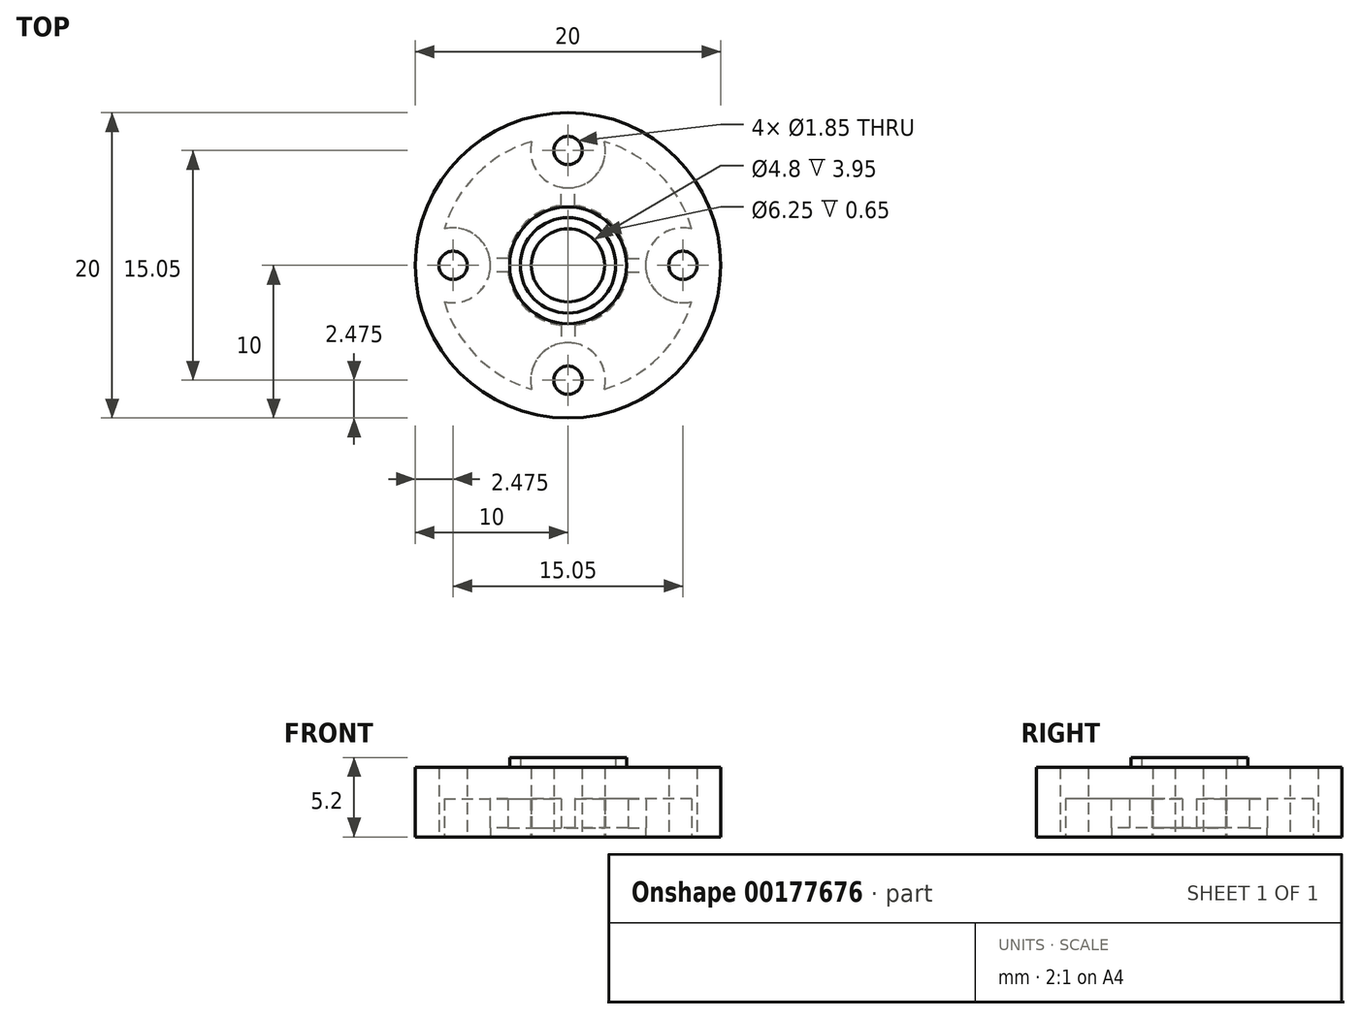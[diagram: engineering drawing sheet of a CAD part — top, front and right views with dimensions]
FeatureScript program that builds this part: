
annotation { "Feature Type Name" : "Feature", "Feature Type Description" : "" }
export const myFeature = defineFeature(function(context is Context, id is Id, definition is map)
    precondition{}
    {
        {
            var Q0;
            Q0=qCreatedBy(makeId("Top.planeOp"),FACE);
            var sketch = newSketch(context, id + "F0", { "sketchPlane" : qUnion([Q0])});
            skCircle(sketch, "E0", {"center": v(0, 0) * mm, "radius": 10 * mm});
            skSolve(sketch);
        }
        {
            var Q0;
            Q0=qSketchRegion(id+"F0",true);
            extrude(context, id + "F1", {"entities" : qUnion([Q0]), "depth" : 4.55 * mm});
        }
        {
            var Q0;
            Q0=makeQuery(id+"F1.opExtrude","CAP_FACE",FACE,{"disambiguationData":[OSD([sQuery(id+"F0.wireOp",EDGE,"E0")])],"isStart":true});
            var sketch = newSketch(context, id + "F2", { "sketchPlane" : qUnion([Q0])});
            skCircle(sketch, "E1", {"center": v(0, 0) * mm, "radius": 8.45 * mm});
            skCircle(sketch, "E2", {"center": v(0, 0) * mm, "radius": 3.95 * mm});
            skCircle(sketch, "E3", {"center": v(0, 0) * mm, "radius": 2.4 * mm});
            skLineSegment(sketch, "E4", {"start": v(0, 8.45) * mm, "end": v(0, -8.45) * mm, "construction": true});
            skLineSegment(sketch, "E5", {"start": v(8.45, 0) * mm, "end": v(-8.45, 0) * mm, "construction": true});
            skLineSegment(sketch, "E6", {"start": v(0.45, 3.92) * mm, "end": v(0.45, 5.12) * mm});
            skLineSegment(sketch, "E7", {"start": v(-0.45, 3.92) * mm, "end": v(-0.45, 5.12) * mm});
            skLineSegment(sketch, "E8", {"start": v(3.92, 0.45) * mm, "end": v(5.12, 0.45) * mm});
            skLineSegment(sketch, "E9", {"start": v(3.92, -0.45) * mm, "end": v(5.12, -0.45) * mm});
            skLineSegment(sketch, "E10", {"start": v(0.45, -3.92) * mm, "end": v(0.45, -5.12) * mm});
            skLineSegment(sketch, "E11", {"start": v(-0.45, -3.92) * mm, "end": v(-0.45, -5.12) * mm});
            skLineSegment(sketch, "E12", {"start": v(-3.92, -0.45) * mm, "end": v(-5.12, -0.45) * mm});
            skLineSegment(sketch, "E13", {"start": v(-3.92, 0.45) * mm, "end": v(-5.12, 0.45) * mm});
            skCircle(sketch, "E14", {"center": v(7.52, 0) * mm, "radius": 0.93 * mm});
            skCircle(sketch, "E15", {"center": v(7.52, 0) * mm, "radius": 2.45 * mm});
            skCircle(sketch, "E16.1.0", {"center": v(0, 7.52) * mm, "radius": 0.93 * mm});
            skCircle(sketch, "E16.1.1", {"center": v(0, 7.52) * mm, "radius": 2.45 * mm});
            skCircle(sketch, "E16.2.0", {"center": v(-7.52, 0) * mm, "radius": 0.93 * mm});
            skCircle(sketch, "E16.2.1", {"center": v(-7.52, 0) * mm, "radius": 2.45 * mm});
            skCircle(sketch, "E16.3.0", {"center": v(0, -7.52) * mm, "radius": 0.93 * mm});
            skCircle(sketch, "E16.3.1", {"center": v(0, -7.52) * mm, "radius": 2.45 * mm});
            skLineSegment(sketch, "E17.trimOffspring", {"start": v(8.33, -0.45) * mm, "end": v(8.44, -0.45) * mm});
            skLineSegment(sketch, "E18.trimOffspring", {"start": v(8.33, 0.45) * mm, "end": v(8.44, 0.45) * mm});
            skLineSegment(sketch, "E19.trimOffspring", {"start": v(-0.45, -8.33) * mm, "end": v(-0.45, -8.44) * mm});
            skLineSegment(sketch, "E20.trimOffspring", {"start": v(0.45, -8.33) * mm, "end": v(0.45, -8.44) * mm});
            skLineSegment(sketch, "E21.trimOffspring", {"start": v(-8.33, -0.45) * mm, "end": v(-8.44, -0.45) * mm});
            skLineSegment(sketch, "E22.trimOffspring", {"start": v(-8.33, 0.45) * mm, "end": v(-8.44, 0.45) * mm});
            skLineSegment(sketch, "E23.trimOffspring", {"start": v(-0.45, 8.33) * mm, "end": v(-0.45, 8.44) * mm});
            skLineSegment(sketch, "E24.trimOffspring", {"start": v(0.45, 8.33) * mm, "end": v(0.45, 8.44) * mm});
            skSolve(sketch);
        }
        {
            var Q0;
            {var subQ6=sQuery(id+"F2.wireOp",EDGE,"E6");Q0=makeQuery(id+"F2.imprint","IMPRINT",FACE,{"disambiguationData":[TD([[makeQuery(id+"F2.imprint","IMPRINT",EDGE,{"derivedFrom":subQ6}),-1.0]])]});}
            var Q1;
            {var subQ6=sQuery(id+"F2.wireOp",EDGE,"E7");Q1=makeQuery(id+"F2.imprint","IMPRINT",FACE,{"disambiguationData":[TD([[makeQuery(id+"F2.imprint","IMPRINT",EDGE,{"derivedFrom":subQ6}),1.0]])]});}
            var Q2;
            {var subQ0=sQuery(id+"F2.wireOp",EDGE,"E11");Q2=makeQuery(id+"F2.imprint","IMPRINT",FACE,{"disambiguationData":[TD([[makeQuery(id+"F2.imprint","IMPRINT",EDGE,{"derivedFrom":subQ0}),-1.0]])]});}
            var Q3;
            {var subQ1=sQuery(id+"F2.wireOp",EDGE,"E9");Q3=makeQuery(id+"F2.imprint","IMPRINT",FACE,{"disambiguationData":[TD([[makeQuery(id+"F2.imprint","IMPRINT",EDGE,{"derivedFrom":subQ1}),-1.0]])]});}
            var Q4;
            {var subQ0=sQuery(id+"F2.wireOp",EDGE,"E14");var subQ1=makeQuery(id+"F2.imprint","INTERSECT",VERTEX,{"derivedFrom":[subQ0,sQuery(id+"F2.wireOp",EDGE,"E18.trimOffspring")]});Q4=makeQuery(id+"F2.imprint","IMPRINT",FACE,{"disambiguationData":[TD([[makeQuery(id+"F2.imprint","IMPRINT",EDGE,{"disambiguationData":[TD([[subQ1,1.0]])],"derivedFrom":subQ0}),1.0]])]});}
            var Q5;
            {var subQ0=sQuery(id+"F2.wireOp",EDGE,"E16.2.0");var subQ1=makeQuery(id+"F2.imprint","INTERSECT",VERTEX,{"derivedFrom":[subQ0,sQuery(id+"F2.wireOp",EDGE,"E21.trimOffspring")]});Q5=makeQuery(id+"F2.imprint","IMPRINT",FACE,{"disambiguationData":[TD([[makeQuery(id+"F2.imprint","IMPRINT",EDGE,{"disambiguationData":[TD([[subQ1,1.0]])],"derivedFrom":subQ0}),1.0]])]});}
            var Q6;
            {var subQ0=sQuery(id+"F2.wireOp",EDGE,"E16.1.0");var subQ1=makeQuery(id+"F2.imprint","INTERSECT",VERTEX,{"derivedFrom":[subQ0,sQuery(id+"F2.wireOp",EDGE,"E23.trimOffspring")]});Q6=makeQuery(id+"F2.imprint","IMPRINT",FACE,{"disambiguationData":[TD([[makeQuery(id+"F2.imprint","IMPRINT",EDGE,{"disambiguationData":[TD([[subQ1,1.0]])],"derivedFrom":subQ0}),1.0]])]});}
            var Q7;
            {var subQ0=sQuery(id+"F2.wireOp",EDGE,"E16.3.0");var subQ1=makeQuery(id+"F2.imprint","INTERSECT",VERTEX,{"derivedFrom":[subQ0,sQuery(id+"F2.wireOp",EDGE,"E20.trimOffspring")]});Q7=makeQuery(id+"F2.imprint","IMPRINT",FACE,{"disambiguationData":[TD([[makeQuery(id+"F2.imprint","IMPRINT",EDGE,{"disambiguationData":[TD([[subQ1,1.0]])],"derivedFrom":subQ0}),1.0]])]});}
            var Q8;
            Q8=makeQuery(id+"F2.imprint","IMPRINT",FACE,{"disambiguationData":[TD([[makeQuery(id+"F2.imprint","IMPRINT",EDGE,{"derivedFrom":sQuery(id+"F2.wireOp",EDGE,"E3")}),1.0]])]});
            extrude(context, id + "F3", {"entities" : qUnion([Q0, Q1, Q2, Q3, Q4, Q5, Q6, Q7, Q8]), "operationType" : NewBodyOperationType.REMOVE, "oppositeDirection" : true, "depth" : 2.5 * mm});
        }
        {
            var Q0;
            Q0=makeQuery(id+"F3.boolean.opBoolean","COPY",FACE,{"derivedFrom":makeQuery(id+"F3.opExtrude","CAP_FACE",FACE,{"disambiguationData":[OSD([sQuery(id+"F2.wireOp",EDGE,"E14")])],"isStart":false})});
            var Q1;
            Q1=makeQuery(id+"F3.boolean.opBoolean","COPY",FACE,{"derivedFrom":makeQuery(id+"F3.opExtrude","CAP_FACE",FACE,{"disambiguationData":[OSD([sQuery(id+"F2.wireOp",EDGE,"E16.2.0")])],"isStart":false})});
            var Q2;
            Q2=makeQuery(id+"F3.boolean.opBoolean","COPY",FACE,{"derivedFrom":makeQuery(id+"F3.opExtrude","CAP_FACE",FACE,{"disambiguationData":[OSD([sQuery(id+"F2.wireOp",EDGE,"E16.1.0")])],"isStart":false})});
            var Q3;
            Q3=makeQuery(id+"F3.boolean.opBoolean","COPY",FACE,{"derivedFrom":makeQuery(id+"F3.opExtrude","CAP_FACE",FACE,{"disambiguationData":[OSD([sQuery(id+"F2.wireOp",EDGE,"E3")])],"isStart":false})});
            var Q4;
            Q4=makeQuery(id+"F3.boolean.opBoolean","COPY",FACE,{"derivedFrom":makeQuery(id+"F3.opExtrude","CAP_FACE",FACE,{"disambiguationData":[OSD([sQuery(id+"F2.wireOp",EDGE,"E16.3.0")])],"isStart":false})});
            extrude(context, id + "F4", {"entities" : qUnion([Q0, Q1, Q2, Q3, Q4]), "operationType" : NewBodyOperationType.REMOVE, "oppositeDirection" : true, "depth" : 25 * mm});
        }
        {
            var Q0;
            Q0=makeQuery(id+"F2.imprint","IMPRINT",FACE,{"disambiguationData":[TD([[makeQuery(id+"F2.imprint","IMPRINT",EDGE,{"derivedFrom":sQuery(id+"F2.wireOp",EDGE,"E3")}),-1.0]])]});
            var Q1;
            {var subQ0=sQuery(id+"F2.wireOp",EDGE,"E6");Q1=makeQuery(id+"F2.imprint","IMPRINT",FACE,{"disambiguationData":[TD([[makeQuery(id+"F2.imprint","IMPRINT",EDGE,{"derivedFrom":subQ0}),1.0]])]});}
            var Q2;
            {var subQ0=sQuery(id+"F2.wireOp",EDGE,"E8");Q2=makeQuery(id+"F2.imprint","IMPRINT",FACE,{"disambiguationData":[TD([[makeQuery(id+"F2.imprint","IMPRINT",EDGE,{"derivedFrom":subQ0}),-1.0]])]});}
            var Q3;
            {var subQ0=sQuery(id+"F2.wireOp",EDGE,"E10");Q3=makeQuery(id+"F2.imprint","IMPRINT",FACE,{"disambiguationData":[TD([[makeQuery(id+"F2.imprint","IMPRINT",EDGE,{"derivedFrom":subQ0}),-1.0]])]});}
            var Q4;
            {var subQ0=sQuery(id+"F2.wireOp",EDGE,"E12");Q4=makeQuery(id+"F2.imprint","IMPRINT",FACE,{"disambiguationData":[TD([[makeQuery(id+"F2.imprint","IMPRINT",EDGE,{"derivedFrom":subQ0}),-1.0]])]});}
            extrude(context, id + "F5", {"entities" : qUnion([Q0, Q1, Q2, Q3, Q4]), "operationType" : NewBodyOperationType.REMOVE, "oppositeDirection" : true, "depth" : .6 * mm});
        }
        {
            var Q0;
            Q0=makeQuery(id+"F1.opExtrude","CAP_FACE",FACE,{"disambiguationData":[OSD([sQuery(id+"F0.wireOp",EDGE,"E0")])],"isStart":false});
            var sketch = newSketch(context, id + "F6", { "sketchPlane" : qUnion([Q0])});
            skCircle(sketch, "E25", {"center": v(0, 0) * mm, "radius": 3.83 * mm});
            skCircle(sketch, "E26", {"center": v(0, 0) * mm, "radius": 3.12 * mm});
            skSolve(sketch);
        }
        {
            var Q0;
            Q0=qSketchRegion(id+"F6",true);
            extrude(context, id + "F7", {"entities" : qUnion([Q0]), "operationType" : NewBodyOperationType.ADD, "depth" : .65 * mm});
        }
    });
